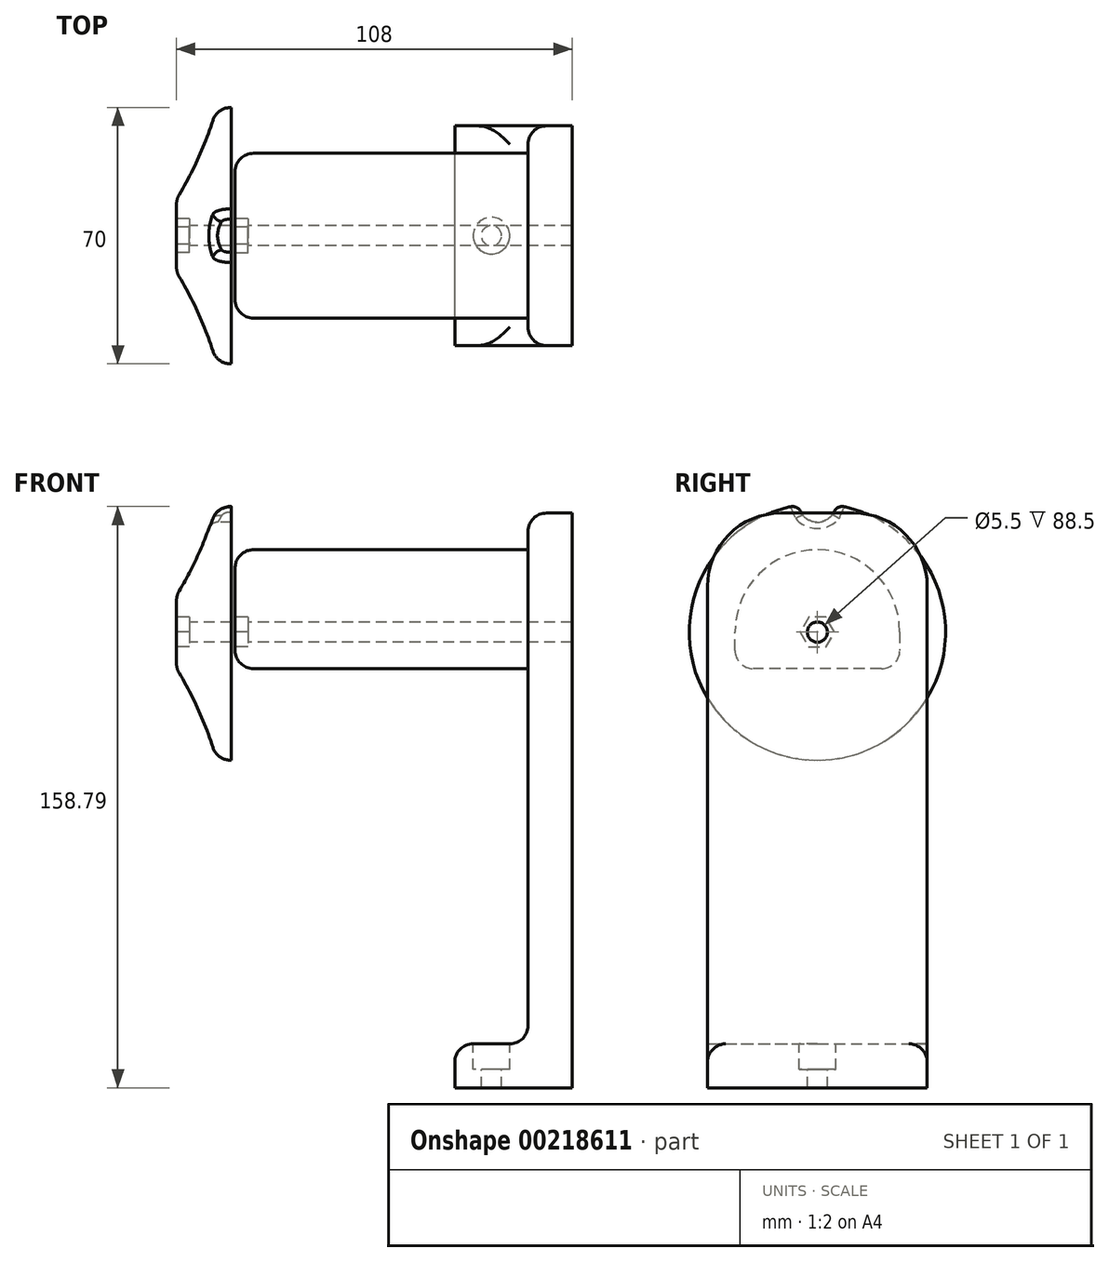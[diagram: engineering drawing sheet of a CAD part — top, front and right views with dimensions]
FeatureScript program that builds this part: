
annotation { "Feature Type Name" : "Feature", "Feature Type Description" : "" }
export const myFeature = defineFeature(function(context is Context, id is Id, definition is map)
    precondition{}
    {
        {
            var Q0;
            Q0=qCreatedBy(makeId("Front.planeOp"),FACE);
            var sketch = newSketch(context, id + "F0", { "sketchPlane" : qUnion([Q0])});
            skLineSegment(sketch, "E0", {"start": v(0, 0) * mm, "end": v(32, 0) * mm});
            skLineSegment(sketch, "E1", {"start": v(32, 0) * mm, "end": v(32, 157) * mm});
            skLineSegment(sketch, "E2", {"start": v(32, 157) * mm, "end": v(20, 157) * mm});
            skLineSegment(sketch, "E3", {"start": v(20, 157) * mm, "end": v(20, 12) * mm});
            skLineSegment(sketch, "E4", {"start": v(20, 12) * mm, "end": v(0, 12) * mm});
            skLineSegment(sketch, "E5", {"start": v(0, 12) * mm, "end": v(0, 0) * mm});
            skSolve(sketch);
        }
        {
            var Q0;
            Q0 = qSketchRegion(id + "F0", true);
            extrude(context, id + "F1", {"entities" : qUnion([Q0]), "depth" : 60 * mm, "offsetDistance" : 25 * mm, "symmetric" : true});
        }
        {
            var Q0;
            Q0=makeQuery(id+"F1.opExtrude","SWEPT_FACE",FACE,{"disambiguationData":[OSD([sQuery(id+"F0.wireOp",EDGE,"E3")])]});
            var sketch = newSketch(context, id + "F2", { "sketchPlane" : qUnion([Q0])});
            skArc(sketch, "E6", {"start": v(22.5, 124.5) * mm, "mid": v(0, 147) * mm, "end": v(-22.5, 124.5) * mm});
            skLineSegment(sketch, "E7", {"start": v(-22.5, 124.5) * mm, "end": v(-22.5, 114.5) * mm});
            skLineSegment(sketch, "E8", {"start": v(-22.5, 114.5) * mm, "end": v(22.5, 114.5) * mm});
            skLineSegment(sketch, "E9", {"start": v(22.5, 114.5) * mm, "end": v(22.5, 124.5) * mm});
            skSolve(sketch);
        }
        {
            var Q0;
            Q0 = qSketchRegion(id + "F2", true);
            extrude(context, id + "F3", {"entities" : qUnion([Q0]), "operationType" : NewBodyOperationType.ADD, "depth" : 80 * mm, "offsetDistance" : 25 * mm});
        }
        {
            var Q0;
            Q0=makeQuery(id+"F1.opExtrude","SWEPT_FACE",FACE,{"disambiguationData":[OSD([sQuery(id+"F0.wireOp",EDGE,"E4")])]});
            var sketch = newSketch(context, id + "F4", { "sketchPlane" : qUnion([Q0])});
            skCircle(sketch, "E10", {"center": v(10, 0) * mm, "radius": 2.75 * mm});
            skSolve(sketch);
        }
        {
            var Q0;
            Q0 = qSketchRegion(id + "F4", true);
            extrude(context, id + "F5", {"entities" : qUnion([Q0]), "operationType" : NewBodyOperationType.REMOVE, "endBound" : BoundingType.THROUGH_ALL, "oppositeDirection" : true, "depth" : 25 * mm, "offsetDistance" : 25 * mm});
        }
        {
            var Q0;
            Q0=makeQuery(id+"F1.opExtrude","SWEPT_FACE",FACE,{"disambiguationData":[OSD([sQuery(id+"F0.wireOp",EDGE,"E4")])]});
            var sketch = newSketch(context, id + "F6", { "sketchPlane" : qUnion([Q0])});
            skCircle(sketch, "E11", {"center": v(10, 0) * mm, "radius": 5 * mm});
            skSolve(sketch);
        }
        {
            var Q0;
            Q0 = qSketchRegion(id + "F6", true);
            extrude(context, id + "F7", {"entities" : qUnion([Q0]), "operationType" : NewBodyOperationType.REMOVE, "oppositeDirection" : true, "depth" : 7 * mm, "offsetDistance" : 25 * mm});
        }
        {
            var Q0;
            Q0=makeQuery(id+"F1.opExtrude","CAP_EDGE",EDGE,{"disambiguationData":[OSD([sQuery(id+"F0.wireOp",EDGE,"E2")])],"isStart":false});
            var Q1;
            Q1=makeQuery(id+"F1.opExtrude","CAP_EDGE",EDGE,{"disambiguationData":[OSD([sQuery(id+"F0.wireOp",EDGE,"E2")])],"isStart":true});
            fillet(context, id + "F8", {"entities" : qUnion([Q0, Q1]), "radius" : 20 * mm, "tangentPropagation" : true, "allowEdgeOverflow" : false});
        }
        {
            var Q0;
            Q0=makeQuery(id+"F3.opExtrude","CAP_FACE",FACE,{"disambiguationData":[OSD([sQuery(id+"F2.wireOp",EDGE,"E6")])],"isStart":false});
            var sketch = newSketch(context, id + "F9", { "sketchPlane" : qUnion([Q0])});
            skCircle(sketch, "E12", {"center": v(0, 124.5) * mm, "radius": 2.75 * mm});
            skSolve(sketch);
        }
        {
            var Q0;
            Q0 = qSketchRegion(id + "F9", true);
            extrude(context, id + "F10", {"entities" : qUnion([Q0]), "operationType" : NewBodyOperationType.REMOVE, "oppositeDirection" : true, "depth" : 15 * mm, "offsetDistance" : 25 * mm});
        }
        {
            var Q0;
            Q0=makeQuery(id+"F3.opExtrude","CAP_FACE",FACE,{"disambiguationData":[OSD([sQuery(id+"F2.wireOp",EDGE,"E6")])],"isStart":false});
            var sketch = newSketch(context, id + "F11", { "sketchPlane" : qUnion([Q0])});
            skCircle(sketch, "E13.cCircle", {"center": v(0, 124.5) * mm, "radius": 4.08 * mm, "construction": true});
            skLineSegment(sketch, "E13.0", {"start": v(4.7, 124.5) * mm, "end": v(2.35, 120.42) * mm});
            skLineSegment(sketch, "E13.1", {"start": v(2.35, 120.42) * mm, "end": v(-2.35, 120.42) * mm});
            skLineSegment(sketch, "E13.2", {"start": v(-2.35, 120.43) * mm, "end": v(-4.7, 124.5) * mm});
            skLineSegment(sketch, "E13.3", {"start": v(-4.7, 124.5) * mm, "end": v(-2.35, 128.57) * mm});
            skLineSegment(sketch, "E13.4", {"start": v(-2.35, 128.57) * mm, "end": v(2.35, 128.57) * mm});
            skLineSegment(sketch, "E13.5", {"start": v(2.35, 128.57) * mm, "end": v(4.7, 124.5) * mm});
            skPoint(sketch, "E13.0.midPoint", {"position": v(3.53, 122.46) * mm});
            skSolve(sketch);
        }
        {
            var Q0;
            Q0 = qSketchRegion(id + "F11", true);
            extrude(context, id + "F12", {"entities" : qUnion([Q0]), "operationType" : NewBodyOperationType.REMOVE, "oppositeDirection" : true, "depth" : 3.5 * mm, "offsetDistance" : 25 * mm});
        }
        {
            var Q0;
            Q0=qCreatedBy(makeId("Front.planeOp"),FACE);
            var sketch = newSketch(context, id + "F13", { "sketchPlane" : qUnion([Q0])});
            skLineSegment(sketch, "E14", {"start": v(-61, 124.5) * mm, "end": v(-61, 159.5) * mm});
            skLineSegment(sketch, "E15", {"start": v(-61, 159.5) * mm, "end": v(-65, 159.5) * mm});
            skArc(sketch, "E16", {"start": v(-76, 134.5) * mm, "mid": v(-69.64, 146.62) * mm, "end": v(-65, 159.5) * mm});
            skLineSegment(sketch, "E17", {"start": v(-76, 134.5) * mm, "end": v(-76, 124.5) * mm});
            skLineSegment(sketch, "E18", {"start": v(-76, 124.5) * mm, "end": v(-61, 124.5) * mm});
            skLineSegment(sketch, "E19", {"start": v(-76, 124.5) * mm, "end": v(-98.93, 124.5) * mm, "construction": true});
            skSolve(sketch);
        }
        {
            var Q0;
            Q0=makeQuery(id+"F13.imprint","IMPRINT",FACE,{"disambiguationData":[TD([[makeQuery(id+"F13.imprint","IMPRINT",EDGE,{"derivedFrom":sQuery(id+"F13.wireOp",EDGE,"E14")}),1.0]])]});
            var Q1;
            Q1=sQuery(id+"F13.wireOp",EDGE,"E19");
            revolve(context, id + "F14", {"entities" : qUnion([Q0]), "axis" : qUnion([Q1]), "revolveType" : RevolveType.FULL});
        }
        {
            var Q0;
            Q0=makeQuery(id+"F14.opRevolve","SWEPT_EDGE",EDGE,{"disambiguationData":[OSD([sQuery(id+"F13.wireOp",EDGE,"E16"),sQuery(id+"F13.wireOp",EDGE,"E17")])]});
            var Q1;
            Q1=makeQuery(id+"F14.opRevolve","SWEPT_EDGE",EDGE,{"disambiguationData":[OSD([sQuery(id+"F13.wireOp",EDGE,"E15"),sQuery(id+"F13.wireOp",EDGE,"E16")])]});
            fillet(context, id + "F15", {"entities" : qUnion([Q0, Q1]), "radius" : 5 * mm, "tangentPropagation" : true, "allowEdgeOverflow" : false});
        }
        {
            var Q0;
            Q0=makeQuery(id+"F14.opRevolve","SWEPT_FACE",FACE,{"disambiguationData":[OSD([sQuery(id+"F13.wireOp",EDGE,"E17")])]});
            var sketch = newSketch(context, id + "F16", { "sketchPlane" : qUnion([Q0])});
            skCircle(sketch, "E20", {"center": v(0, 159.5) * mm, "radius": 5 * mm});
            skSolve(sketch);
        }
        {
            var Q0;
            Q0 = qSketchRegion(id + "F16", true);
            extrude(context, id + "F17", {"entities" : qUnion([Q0]), "operationType" : NewBodyOperationType.REMOVE, "oppositeDirection" : true, "depth" : 25 * mm, "offsetDistance" : 25 * mm});
        }
        {
            var Q0;
            Q0=makeQuery(id+"F17.boolean.opBoolean","INTERSECT",EDGE,{"disambiguationData":[OD(1.0)],"derivedFrom":[makeQuery(id+"F15.opFillet","BLEND_FACE",FACE,{"disambiguationData":[OSD([sQuery(id+"F13.wireOp",EDGE,"E15"),sQuery(id+"F13.wireOp",EDGE,"E16")])]}),makeQuery(id+"F17.opExtrude","SWEPT_FACE",FACE,{"disambiguationData":[OSD([sQuery(id+"F16.wireOp",EDGE,"E20")])]})]});
            fillet(context, id + "F18", {"entities" : qUnion([Q0]), "radius" : 2.5 * mm, "tangentPropagation" : true, "allowEdgeOverflow" : false});
        }
        {
            var Q0;
            Q0=makeQuery(id+"F14.opRevolve","SWEPT_FACE",FACE,{"disambiguationData":[OSD([sQuery(id+"F13.wireOp",EDGE,"E17")])]});
            var sketch = newSketch(context, id + "F19", { "sketchPlane" : qUnion([Q0])});
            skCircle(sketch, "E21.cCircle", {"center": v(0, 124.5) * mm, "radius": 4.05 * mm, "construction": true});
            skLineSegment(sketch, "E21.0", {"start": v(4.68, 124.5) * mm, "end": v(2.34, 120.45) * mm});
            skLineSegment(sketch, "E21.1", {"start": v(2.34, 120.45) * mm, "end": v(-2.34, 120.45) * mm});
            skLineSegment(sketch, "E21.2", {"start": v(-2.34, 120.45) * mm, "end": v(-4.68, 124.5) * mm});
            skLineSegment(sketch, "E21.3", {"start": v(-4.68, 124.5) * mm, "end": v(-2.34, 128.55) * mm});
            skLineSegment(sketch, "E21.4", {"start": v(-2.34, 128.55) * mm, "end": v(2.34, 128.55) * mm});
            skLineSegment(sketch, "E21.5", {"start": v(2.34, 128.55) * mm, "end": v(4.68, 124.5) * mm});
            skPoint(sketch, "E21.0.midPoint", {"position": v(3.5, 122.47) * mm});
            skSolve(sketch);
        }
        {
            var Q0;
            Q0 = qSketchRegion(id + "F19", true);
            extrude(context, id + "F20", {"entities" : qUnion([Q0]), "operationType" : NewBodyOperationType.REMOVE, "oppositeDirection" : true, "depth" : 3.5 * mm, "offsetDistance" : 25 * mm});
        }
        {
            var Q0;
            Q0=makeQuery(id+"F20.boolean.opBoolean","COPY",FACE,{"derivedFrom":makeQuery(id+"F20.opExtrude","CAP_FACE",FACE,{"disambiguationData":[OSD([sQuery(id+"F19.wireOp",EDGE,"E21.0"),sQuery(id+"F19.wireOp",EDGE,"E21.1"),sQuery(id+"F19.wireOp",EDGE,"E21.2"),sQuery(id+"F19.wireOp",EDGE,"E21.3"),sQuery(id+"F19.wireOp",EDGE,"E21.4"),sQuery(id+"F19.wireOp",EDGE,"E21.5")])],"isStart":false})});
            var sketch = newSketch(context, id + "F21", { "sketchPlane" : qUnion([Q0])});
            skCircle(sketch, "E22", {"center": v(0, 124.5) * mm, "radius": 2.75 * mm});
            skPoint(sketch, "E22.centerSnap0", {"position": v(0, 128.55) * mm});
            skSolve(sketch);
        }
        {
            var Q0;
            Q0 = qSketchRegion(id + "F21", true);
            extrude(context, id + "F22", {"entities" : qUnion([Q0]), "operationType" : NewBodyOperationType.REMOVE, "endBound" : BoundingType.THROUGH_ALL, "oppositeDirection" : true, "depth" : 25 * mm, "offsetDistance" : 25 * mm});
        }
        {
            var Q0;
            Q0=makeQuery(id+"F3.opExtrude","CAP_EDGE",EDGE,{"disambiguationData":[OSD([sQuery(id+"F2.wireOp",EDGE,"E8")])],"isStart":true});
            var Q1;
            Q1=makeQuery(id+"F3.opExtrude","SWEPT_EDGE",EDGE,{"disambiguationData":[OSD([sQuery(id+"F2.wireOp",EDGE,"E8"),sQuery(id+"F2.wireOp",EDGE,"E9")])]});
            var Q2;
            Q2=makeQuery(id+"F3.opExtrude","SWEPT_EDGE",EDGE,{"disambiguationData":[OSD([sQuery(id+"F2.wireOp",EDGE,"E7"),sQuery(id+"F2.wireOp",EDGE,"E8")])]});
            fillet(context, id + "F23", {"entities" : qUnion([Q0, Q1, Q2]), "radius" : 5 * mm, "tangentPropagation" : true, "allowEdgeOverflow" : false});
        }
        {
            var Q0;
            Q0=makeQuery(id+"F1.opExtrude","SWEPT_EDGE",EDGE,{"disambiguationData":[OSD([sQuery(id+"F0.wireOp",EDGE,"E3"),sQuery(id+"F0.wireOp",EDGE,"E4")])]});
            var Q1;
            Q1=makeQuery(id+"F1.opExtrude","CAP_EDGE",EDGE,{"disambiguationData":[OSD([sQuery(id+"F0.wireOp",EDGE,"E3")])],"isStart":true});
            var Q2;
            Q2=makeQuery(id+"F1.opExtrude","CAP_EDGE",EDGE,{"disambiguationData":[OSD([sQuery(id+"F0.wireOp",EDGE,"E3")])],"isStart":false});
            var Q3;
            Q3=makeQuery(id+"F1.opExtrude","SWEPT_EDGE",EDGE,{"disambiguationData":[OSD([sQuery(id+"F0.wireOp",EDGE,"E4"),sQuery(id+"F0.wireOp",EDGE,"E5")])]});
            var Q4;
            Q4=makeQuery(id+"F3.opExtrude","CAP_EDGE",EDGE,{"disambiguationData":[OSD([sQuery(id+"F2.wireOp",EDGE,"E6")])],"isStart":false});
            fillet(context, id + "F24", {"entities" : qUnion([Q0, Q1, Q2, Q3, Q4]), "radius" : 5 * mm, "tangentPropagation" : true, "allowEdgeOverflow" : false});
        }
    });
